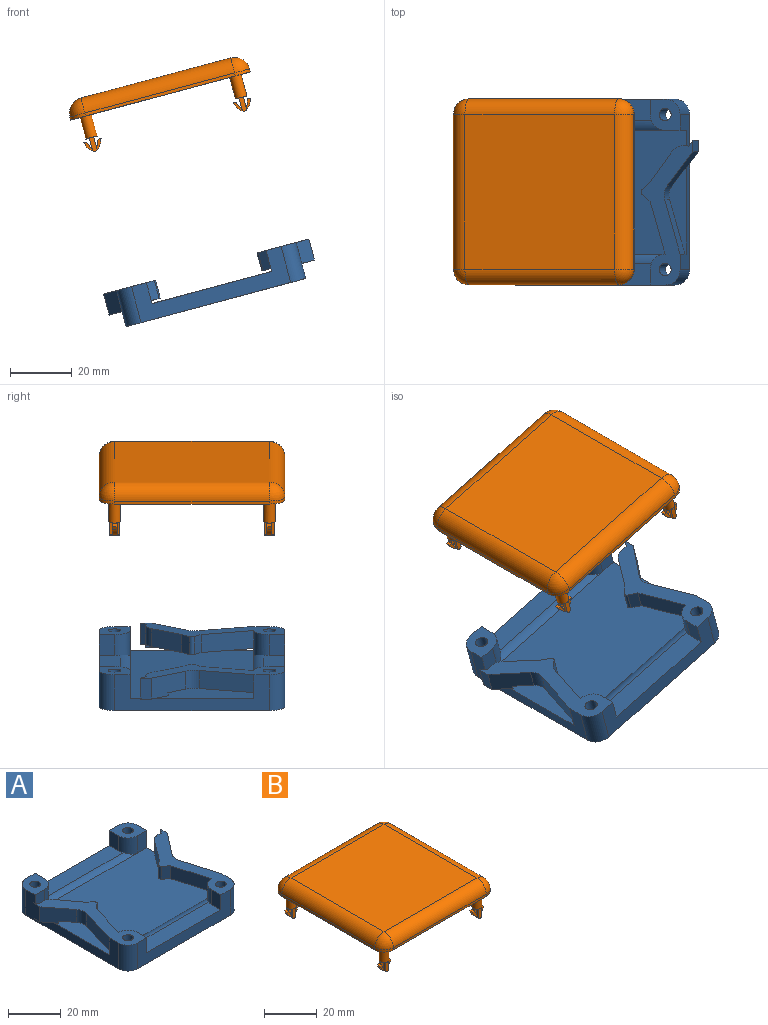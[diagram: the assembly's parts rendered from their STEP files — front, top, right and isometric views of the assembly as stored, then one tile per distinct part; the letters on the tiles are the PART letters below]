
ASSEMBLY  parts=2 mates=1
PART A: 70 faces, bbox 68.6x60x12 mm
  f0: plane 60x60mm, normal (0,0,-1), area 3424.6mm2, adj f8,f11,f12,f13,f48,f49,f50,f51
  f1: cylinder r=2mm len=8mm, axis (0,0,1), area 100.5mm2, adj f40,f69
  f2: cylinder r=2mm len=8mm, axis (0,0,1), area 100.5mm2, adj f38,f67
  f3: cylinder r=2mm len=8mm, axis (0,0,1), area 100.5mm2, adj f27,f65
  f4: cylinder r=2mm len=8mm, axis (0,0,1), area 100.5mm2, adj f16,f63
  f5: plane 5x2mm, normal (0,1,0), area 10mm2, adj f12,f44,f45,f57
  f6: plane 8x5mm, normal (0,-1,0), area 40mm2, adj f8,f16,f45,f61
  f7: plane 40.84x7mm, normal (0,0,1), area 280.5mm2, adj f11,f19,f34,f56,f57,f59
  f8: plane 50x12mm, normal (-1,0,0), area 280mm2, adj f0,f6,f16,f18,f20,f27,f45,f48
  f9: plane 11.04x8.59mm, normal (0.79,-0.61,0), area 91mm2, adj f29,f36,f38,f43,f44,f52
  f10: plane 40.84x7mm, normal (0,0,1), area 280.5mm2, adj f13,f15,f39,f58,f60,f61
  f11: plane 50x12mm, normal (0,-1,0), area 320mm2, adj f0,f7,f19,f27,f34,f38,f48,f51
  f12: plane 50x12mm, normal (1,0,0), area 280mm2, adj f0,f5,f14,f35,f38,f40,f45,f50
  f13: plane 50x12mm, normal (0,1,0), area 320mm2, adj f0,f10,f15,f16,f39,f40,f49,f50
  f14: plane 8x5mm, normal (0,-1,0), area 40mm2, adj f12,f40,f45,f60
  f15: plane 7x5mm, normal (1,0,0), area 35mm2, adj f10,f13,f16,f61
  f16: plane 10x10mm, normal (0,0,1), area 76.7mm2, adj f4,f6,f8,f13,f15,f49,f61
  f17: plane 11.04x8.59mm, normal (-0.79,-0.61,0), area 91mm2, adj f26,f27,f28,f41,f42,f53
  f18: plane 17.54x6mm, normal (-0.96,0.28,0), area 109.7mm2, adj f8,f27,f42,f53
  f19: plane 7x5mm, normal (1,0,0), area 35mm2, adj f7,f11,f27,f56
  f20: plane 5x2mm, normal (0,1,0), area 10mm2, adj f8,f42,f45,f56
  f21: plane 17.06x6mm, normal (0.96,-0.28,0), area 106.7mm2, adj f22,f27,f42,f56
  f22: plane 6x2.66mm, normal (0.64,-0.77,0), area 20.7mm2, adj f21,f27,f42,f46
  f23: plane 6x2.79mm, normal (0.67,0.74,0), area 22.5mm2, adj f24,f27,f42,f46
  f24: plane 9.66x7.08mm, normal (0.81,0.59,0), area 71.9mm2, adj f23,f27,f42,f54
  f25: plane 7x2.05mm, normal (0.81,0.59,0), area 17.8mm2, adj f26,f27,f28,f54
  f26: plane 7x3.72mm, normal (-1,0,0), area 26mm2, adj f17,f25,f27,f28
  f27: plane 46.78x17.33mm, normal (0,0,1), area 283.7mm2, adj f3,f8,f11,f17,f18,f19,f21,f22
  f28: plane 9.25x4.31mm, normal (0,0,-1), area 21.1mm2, adj f17,f25,f26,f41,f54
  f29: plane 9.25x4.31mm, normal (0,0,-1), area 21.1mm2, adj f9,f36,f37,f43,f55
  f30: plane 9.66x7.08mm, normal (-0.81,0.59,0), area 71.9mm2, adj f31,f38,f44,f55
  f31: plane 6x2.79mm, normal (-0.67,0.74,0), area 22.5mm2, adj f30,f38,f44,f47
  f32: plane 6x2.66mm, normal (-0.64,-0.77,0), area 20.7mm2, adj f33,f38,f44,f47
  f33: plane 17.06x6mm, normal (-0.96,-0.28,0), area 106.7mm2, adj f32,f38,f44,f57
  f34: plane 7x5mm, normal (-1,0,0), area 35mm2, adj f7,f11,f38,f57
  f35: plane 17.54x6mm, normal (0.96,0.28,0), area 109.7mm2, adj f12,f38,f44,f52
  f36: plane 7x3.72mm, normal (1,0,0), area 26mm2, adj f9,f29,f37,f38
  f37: plane 7x2.05mm, normal (-0.81,0.59,0), area 17.8mm2, adj f29,f36,f38,f55
  f38: plane 46.78x17.33mm, normal (0,0,1), area 283.7mm2, adj f2,f9,f11,f12,f30,f31,f32,f33
  f39: plane 7x5mm, normal (-1,0,0), area 35mm2, adj f10,f13,f40,f60
  f40: plane 10x10mm, normal (0,0,1), area 76.7mm2, adj f1,f12,f13,f14,f39,f50,f60
  f41: plane 7.3x1mm, normal (1,0,0), area 7.3mm2, adj f17,f28,f42,f54
  f42: plane 34.84x13.02mm, normal (0,0,-1), area 185.8mm2, adj f17,f18,f20,f21,f22,f23,f24,f41
  f43: plane 7.3x1mm, normal (-1,0,0), area 7.3mm2, adj f9,f29,f44,f55
  f44: plane 34.84x13.02mm, normal (0,0,-1), area 185.8mm2, adj f5,f9,f30,f31,f32,f33,f35,f43
  f45: plane 60x40mm, normal (0,0,1), area 2400mm2, adj f5,f6,f8,f12,f14,f20,f58,f59
  f46: cylinder r=1mm len=6mm, axis (0,0,-1), area 10.3mm2, adj f22,f23,f27,f42
  f47: cylinder r=1mm len=6mm, axis (0,0,-1), area 10.3mm2, adj f31,f32,f38,f44
  f48: cylinder r=5mm len=12mm, axis (0,0,-1), area 94.2mm2, adj f0,f8,f11,f27
  f49: cylinder r=5mm len=12mm, axis (0,0,1), area 94.2mm2, adj f0,f8,f13,f16
  f50: cylinder r=5mm len=12mm, axis (0,0,-1), area 94.2mm2, adj f0,f12,f13,f40
  f51: cylinder r=5mm len=12mm, axis (0,0,1), area 94.2mm2, adj f0,f11,f12,f38
  f52: cylinder r=5mm len=6mm, axis (0,0,1), area 28.4mm2, adj f9,f35,f38,f44
  f53: cylinder r=5mm len=6mm, axis (0,0,1), area 28.4mm2, adj f17,f18,f27,f42
  f54: cylinder r=5mm len=7mm, axis (0,0,-1), area 40.6mm2, adj f24,f25,f27,f28,f41,f42
  f55: cylinder r=5mm len=7mm, axis (0,0,1), area 40.6mm2, adj f29,f30,f37,f38,f43,f44
  f56: cylinder r=5mm len=8mm, axis (0,0,-1), area 57.9mm2, adj f7,f19,f20,f21,f27,f59
  f57: cylinder r=5mm len=8mm, axis (0,0,1), area 57.9mm2, adj f5,f7,f33,f34,f38,f59
  f58: cylinder r=5mm len=50mm, axis (1,0,0), area 140.1mm2, adj f10,f45,f60,f61
  f59: cylinder r=5mm len=50mm, axis (-1,0,0), area 140.1mm2, adj f7,f45,f56,f57
  f60: cylinder r=5mm len=8mm, axis (0,0,-1), area 57.9mm2, adj f10,f14,f39,f40,f58
  f61: cylinder r=5mm len=8mm, axis (0,0,1), area 57.9mm2, adj f6,f10,f15,f16,f58
  f62: cylinder r=3.5mm len=7mm, axis (0,0,-1), area 88mm2, adj f0,f63
  f63: plane 7x7mm, normal (0,0,-1), area 25.9mm2, adj f4,f62
  f64: cylinder r=3.5mm len=7mm, axis (0,0,-1), area 88mm2, adj f0,f65
  f65: plane 7x7mm, normal (0,0,-1), area 25.9mm2, adj f3,f64
  f66: cylinder r=3.5mm len=7mm, axis (0,0,-1), area 88mm2, adj f0,f67
  f67: plane 7x7mm, normal (0,0,-1), area 25.9mm2, adj f2,f66
  f68: cylinder r=3.5mm len=7mm, axis (0,0,-1), area 88mm2, adj f0,f69
  f69: plane 7x7mm, normal (0,0,-1), area 25.9mm2, adj f1,f68
PART B: 122 faces, bbox 60x60x17.9 mm
  f0: plane 3.8x3.49mm, normal (0,0,-1), area 8mm2, adj f32,f100,f101,f102,f103,f117,f118
  f1: plane 1.5x0.15mm, normal (0,0,-1), area 0.2mm2, adj f32,f105
  f2: plane 1.5x0.15mm, normal (0,0,-1), area 0.2mm2, adj f32,f104
  f3: plane 1.5x0.15mm, normal (0,0,-1), area 0.2mm2, adj f33,f92
  f4: plane 3.8x3.49mm, normal (0,0,-1), area 8mm2, adj f33,f91,f93,f94,f96,f98,f99
  f5: plane 3.8x3.49mm, normal (0,0,-1), area 8mm2, adj f37,f56,f57,f58,f59,f73,f74
  f6: plane 1.5x0.15mm, normal (0,0,-1), area 0.2mm2, adj f37,f61
  f7: plane 1.5x0.15mm, normal (0,0,-1), area 0.2mm2, adj f37,f60
  f8: plane 4.28x0.95mm, normal (-1,0,0), area 4.1mm2, adj f13,f38,f49,f52,f54
  f9: plane 4.28x0.95mm, normal (1,0,0), area 4.1mm2, adj f13,f38,f44,f52,f53
  f10: plane 4.28x1.04mm, normal (-1,0,0), area 4.4mm2, adj f13,f39,f48,f51,f54
  f11: plane 4.28x1.04mm, normal (1,0,0), area 4.4mm2, adj f13,f39,f43,f51,f53
  f12: plane 1.5x0.15mm, normal (0,0,-1), area 0.2mm2, adj f35,f39
  f13: plane 3.8x3.49mm, normal (0,0,-1), area 8mm2, adj f8,f9,f10,f11,f35,f51,f52
  f14: plane 50x1mm, normal (0,-1,0), area 50mm2, adj f19,f22,f28,f31
  f15: plane 50x1mm, normal (1,0,0), area 50mm2, adj f19,f25,f29,f31
  f16: plane 50x1mm, normal (0,1,0), area 50mm2, adj f19,f20,f24,f25
  f17: plane 50x1mm, normal (-1,0,0), area 50mm2, adj f19,f20,f22,f23
  f18: plane 50x50mm, normal (0,0,1), area 2500mm2, adj f23,f24,f28,f29
  f19: plane 60x60mm, normal (0,0,-1), area 3533.2mm2, adj f14,f15,f16,f17,f20,f22,f25,f31
  f20: cylinder r=5mm len=5mm, axis (0,0,1), area 7.9mm2, adj f16,f17,f19,f21
  f21: sphere r=5mm, area 39.3mm2, adj f20,f23,f24
  f22: cylinder r=5mm len=5mm, axis (0,0,-1), area 7.9mm2, adj f14,f17,f19,f26
  f23: cylinder r=5mm len=50mm, axis (0,1,0), area 392.7mm2, adj f17,f18,f21,f26
  f24: cylinder r=5mm len=50mm, axis (1,0,0), area 392.7mm2, adj f16,f18,f21,f27
  f25: cylinder r=5mm len=5mm, axis (0,0,-1), area 7.9mm2, adj f15,f16,f19,f27
  f26: sphere r=5mm, area 39.3mm2, adj f22,f23,f28
  f27: sphere r=5mm, area 39.3mm2, adj f24,f25,f29
  f28: cylinder r=5mm len=50mm, axis (-1,0,0), area 392.7mm2, adj f14,f18,f26,f30
  f29: cylinder r=5mm len=50mm, axis (0,-1,0), area 392.7mm2, adj f15,f18,f27,f30
  f30: sphere r=5mm, area 39.3mm2, adj f28,f29,f31
  f31: cylinder r=5mm len=5mm, axis (0,0,1), area 7.9mm2, adj f14,f15,f19,f30
  f32: cylinder r=1.9mm len=7.2mm, axis (0,0,1), area 86mm2, adj f0,f1,f2,f19
  f33: cylinder r=1.9mm len=7.2mm, axis (0,0,1), area 86mm2, adj f3,f4,f19,f34
  f34: plane 1.5x0.15mm, normal (0,0,-1), area 0.2mm2, adj f33,f97
  f35: cylinder r=1.9mm len=7.2mm, axis (0,0,1), area 86mm2, adj f12,f13,f19,f36
  f36: plane 1.5x0.15mm, normal (0,0,-1), area 0.2mm2, adj f35,f38
  f37: cylinder r=1.9mm len=7.2mm, axis (0,0,1), area 86mm2, adj f5,f6,f7,f19
  f38: plane 4.72x1.5mm, normal (0,-1,0), area 6.8mm2, adj f8,f9,f36,f53,f54
  f39: plane 4.72x1.5mm, normal (0,1,0), area 6.8mm2, adj f10,f11,f12,f53,f54
  f40: plane 1.58x1.5mm, normal (-0.92,0,0.39), area 2.6mm2, adj f41,f43,f44,f55
  f41: plane 1.5x1.03mm, normal (0,0,1), area 1.5mm2, adj f40,f42,f43,f44
  f42: plane 1.5x1.14mm, normal (0.92,0,-0.39), area 1.9mm2, adj f41,f43,f44,f53
  f43: plane 3.28x2.21mm, normal (0,1,0), area 2.9mm2, adj f11,f40,f41,f42,f53,f55
  f44: plane 3.28x2.21mm, normal (0,-1,0), area 2.9mm2, adj f9,f40,f41,f42,f53,f55
  f45: plane 1.5x1.14mm, normal (-0.92,0,-0.39), area 1.9mm2, adj f46,f48,f49,f54
  f46: plane 1.5x1.03mm, normal (0,0,1), area 1.5mm2, adj f45,f47,f48,f49
  f47: plane 2.8x1.5mm, normal (0.92,0,0.39), area 4.6mm2, adj f46,f48,f49,f50
  f48: plane 3.28x2.21mm, normal (0,1,0), area 2.8mm2, adj f10,f45,f46,f47,f54
  f49: plane 3.28x2.21mm, normal (0,-1,0), area 2.8mm2, adj f8,f45,f46,f47,f54
  f50: plane 1.5x0.17mm, normal (0,0,1), area 0.3mm2, adj f47,f51,f52,f55
  f51: plane 3.8x1.5mm, normal (0,-1,0), area 5.5mm2, adj f10,f11,f13,f50,f55
  f52: plane 3.8x1.5mm, normal (0,1,0), area 5.5mm2, adj f8,f9,f13,f50,f55
  f53: cylinder r=5mm len=3.49mm, axis (0,-1,0), area 7.2mm2, adj f9,f11,f38,f39,f42,f43,f44,f54
  f54: cylinder r=5mm len=3.49mm, axis (0,-1,0), area 7.2mm2, adj f8,f10,f38,f39,f45,f48,f49,f53
  f55: cylinder r=2mm len=1.84mm, axis (0,1,0), area 3.5mm2, adj f40,f43,f44,f50,f51,f52
  f56: plane 4.28x0.95mm, normal (1,0,0), area 4.1mm2, adj f5,f60,f71,f74,f76
  f57: plane 4.28x0.95mm, normal (-1,0,0), area 4.1mm2, adj f5,f60,f66,f74,f75
  f58: plane 4.28x1.04mm, normal (1,0,0), area 4.4mm2, adj f5,f61,f70,f73,f76
  f59: plane 4.28x1.04mm, normal (-1,0,0), area 4.4mm2, adj f5,f61,f65,f73,f75
  f60: plane 4.72x1.5mm, normal (0,-1,0), area 6.8mm2, adj f7,f56,f57,f75,f76
  f61: plane 4.72x1.5mm, normal (0,1,0), area 6.8mm2, adj f6,f58,f59,f75,f76
  f62: plane 1.58x1.5mm, normal (0.92,0,0.39), area 2.6mm2, adj f63,f65,f66,f77
  f63: plane 1.5x1.03mm, normal (0,0,1), area 1.5mm2, adj f62,f64,f65,f66
  f64: plane 1.5x1.14mm, normal (-0.92,0,-0.39), area 1.9mm2, adj f63,f65,f66,f75
  f65: plane 3.28x2.21mm, normal (0,1,0), area 2.9mm2, adj f59,f62,f63,f64,f75,f77
  f66: plane 3.28x2.21mm, normal (0,-1,0), area 2.9mm2, adj f57,f62,f63,f64,f75,f77
  f67: plane 1.5x1.14mm, normal (0.92,0,-0.39), area 1.9mm2, adj f68,f70,f71,f76
  f68: plane 1.5x1.03mm, normal (0,0,1), area 1.5mm2, adj f67,f69,f70,f71
  f69: plane 2.8x1.5mm, normal (-0.92,0,0.39), area 4.6mm2, adj f68,f70,f71,f72
  f70: plane 3.28x2.21mm, normal (0,1,0), area 2.8mm2, adj f58,f67,f68,f69,f76
  f71: plane 3.28x2.21mm, normal (0,-1,0), area 2.8mm2, adj f56,f67,f68,f69,f76
  f72: plane 1.5x0.17mm, normal (0,0,1), area 0.3mm2, adj f69,f73,f74,f77
  f73: plane 3.8x1.5mm, normal (0,-1,0), area 5.5mm2, adj f5,f58,f59,f72,f77
  f74: plane 3.8x1.5mm, normal (0,1,0), area 5.5mm2, adj f5,f56,f57,f72,f77
  f75: cylinder r=5mm len=3.49mm, axis (0,-1,0), area 7.2mm2, adj f57,f59,f60,f61,f64,f65,f66,f76
  f76: cylinder r=5mm len=3.49mm, axis (0,-1,0), area 7.2mm2, adj f56,f58,f60,f61,f67,f70,f71,f75
  f77: cylinder r=2mm len=1.84mm, axis (0,1,0), area 3.5mm2, adj f62,f65,f66,f72,f73,f74
  f78: plane 1.5x1.03mm, normal (0,0,1), area 1.5mm2, adj f80,f83,f84,f85
  f79: plane 1.5x1.03mm, normal (0,0,1), area 1.5mm2, adj f81,f82,f86,f87
  f80: plane 1.5x1.14mm, normal (-0.92,0,-0.39), area 1.9mm2, adj f78,f84,f85,f88
  f81: plane 1.5x1.14mm, normal (0.92,0,-0.39), area 1.9mm2, adj f79,f86,f87,f89
  f82: plane 2.8x1.5mm, normal (-0.92,0,0.39), area 4.6mm2, adj f79,f86,f87,f90
  f83: plane 1.58x1.5mm, normal (0.92,0,0.39), area 2.6mm2, adj f78,f84,f85,f95
  f84: plane 3.28x2.21mm, normal (0,-1,0), area 2.9mm2, adj f78,f80,f83,f88,f94,f95
  f85: plane 3.28x2.21mm, normal (0,1,0), area 2.9mm2, adj f78,f80,f83,f88,f95,f99
  f86: plane 3.28x2.21mm, normal (0,1,0), area 2.8mm2, adj f79,f81,f82,f89,f98
  f87: plane 3.28x2.21mm, normal (0,-1,0), area 2.8mm2, adj f79,f81,f82,f89,f93
  f88: cylinder r=5mm len=3.49mm, axis (0,1,0), area 7.2mm2, adj f80,f84,f85,f89,f92,f94,f97,f99
  f89: cylinder r=5mm len=3.49mm, axis (0,1,0), area 7.2mm2, adj f81,f86,f87,f88,f92,f93,f97,f98
  f90: plane 1.5x0.17mm, normal (0,0,1), area 0.3mm2, adj f82,f91,f95,f96
  f91: plane 3.8x1.5mm, normal (0,1,0), area 5.5mm2, adj f4,f90,f93,f94,f95
  f92: plane 4.72x1.5mm, normal (0,-1,0), area 6.8mm2, adj f3,f88,f89,f93,f94
  f93: plane 4.28x1.04mm, normal (1,0,0), area 4.4mm2, adj f4,f87,f89,f91,f92
  f94: plane 4.28x1.04mm, normal (-1,0,0), area 4.4mm2, adj f4,f84,f88,f91,f92
  f95: cylinder r=2mm len=1.84mm, axis (0,-1,0), area 3.5mm2, adj f83,f84,f85,f90,f91,f96
  f96: plane 3.8x1.5mm, normal (0,-1,0), area 5.5mm2, adj f4,f90,f95,f98,f99
  f97: plane 4.72x1.5mm, normal (0,1,0), area 6.8mm2, adj f34,f88,f89,f98,f99
  f98: plane 4.28x0.95mm, normal (1,0,0), area 4.1mm2, adj f4,f86,f89,f96,f97
  f99: plane 4.28x0.95mm, normal (-1,0,0), area 4.1mm2, adj f4,f85,f88,f96,f97
  f100: plane 4.28x0.95mm, normal (-1,0,0), area 4.1mm2, adj f0,f104,f115,f118,f120
  f101: plane 4.28x0.95mm, normal (1,0,0), area 4.1mm2, adj f0,f104,f110,f118,f119
  f102: plane 4.28x1.04mm, normal (-1,0,0), area 4.4mm2, adj f0,f105,f114,f117,f120
  f103: plane 4.28x1.04mm, normal (1,0,0), area 4.4mm2, adj f0,f105,f109,f117,f119
  f104: plane 4.72x1.5mm, normal (0,1,0), area 6.8mm2, adj f2,f100,f101,f119,f120
  f105: plane 4.72x1.5mm, normal (0,-1,0), area 6.8mm2, adj f1,f102,f103,f119,f120
  f106: plane 1.58x1.5mm, normal (-0.92,0,0.39), area 2.6mm2, adj f107,f109,f110,f121
  f107: plane 1.5x1.03mm, normal (0,0,1), area 1.5mm2, adj f106,f108,f109,f110
  f108: plane 1.5x1.14mm, normal (0.92,0,-0.39), area 1.9mm2, adj f107,f109,f110,f119
  f109: plane 3.28x2.21mm, normal (0,-1,0), area 2.9mm2, adj f103,f106,f107,f108,f119,f121
  f110: plane 3.28x2.21mm, normal (0,1,0), area 2.9mm2, adj f101,f106,f107,f108,f119,f121
  f111: plane 1.5x1.14mm, normal (-0.92,0,-0.39), area 1.9mm2, adj f112,f114,f115,f120
  f112: plane 1.5x1.03mm, normal (0,0,1), area 1.5mm2, adj f111,f113,f114,f115
  f113: plane 2.8x1.5mm, normal (0.92,0,0.39), area 4.6mm2, adj f112,f114,f115,f116
  f114: plane 3.28x2.21mm, normal (0,-1,0), area 2.8mm2, adj f102,f111,f112,f113,f120
  f115: plane 3.28x2.21mm, normal (0,1,0), area 2.8mm2, adj f100,f111,f112,f113,f120
  f116: plane 1.5x0.17mm, normal (0,0,1), area 0.3mm2, adj f113,f117,f118,f121
  f117: plane 3.8x1.5mm, normal (0,1,0), area 5.5mm2, adj f0,f102,f103,f116,f121
  f118: plane 3.8x1.5mm, normal (0,-1,0), area 5.5mm2, adj f0,f100,f101,f116,f121
  f119: cylinder r=5mm len=3.49mm, axis (0,1,0), area 7.2mm2, adj f101,f103,f104,f105,f108,f109,f110,f120
  f120: cylinder r=5mm len=3.49mm, axis (0,1,0), area 7.2mm2, adj f100,f102,f104,f105,f111,f114,f115,f119
  f121: cylinder r=2mm len=1.84mm, axis (0,-1,0), area 3.5mm2, adj f106,f109,f110,f116,f117,f118
PLACE A rot(axis=(0,-1,0),15deg) t=(-15.72,31.65,12.9)mm
PLACE B rot(axis=(0,-1,0),15deg) t=(-33.59,31.65,79.56)mm
MATE slider B.f20 <-> A.f4  axis (-0.26,0,0.97) through (-56.8,56.65,69.62)mm
